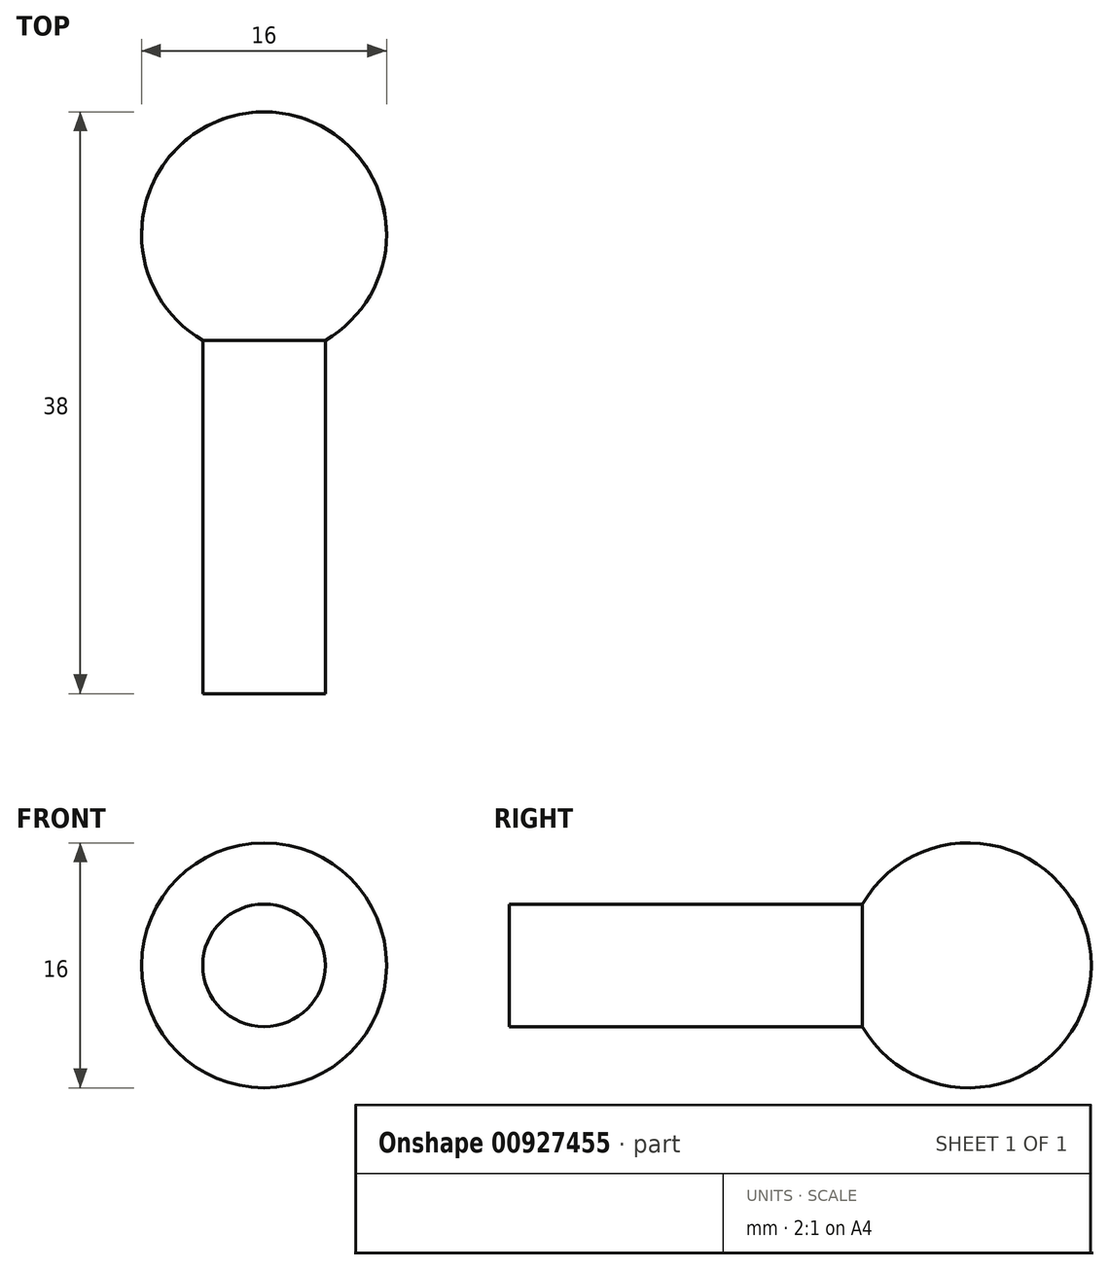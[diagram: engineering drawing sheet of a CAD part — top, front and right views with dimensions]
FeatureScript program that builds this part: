
annotation { "Feature Type Name" : "Feature", "Feature Type Description" : "" }
export const myFeature = defineFeature(function(context is Context, id is Id, definition is map)
    precondition{}
    {
        {
            var Q0;
            Q0=qCreatedBy(makeId("Top.planeOp"),FACE);
            var sketch = newSketch(context, id + "F0", { "sketchPlane" : qUnion([Q0])});
            skArc(sketch, "E0", {"start": v(8, 0) * mm, "mid": v(0, 8) * mm, "end": v(-8, 0) * mm});
            skLineSegment(sketch, "E1", {"start": v(-8, 0) * mm, "end": v(8, 0) * mm});
            skPoint(sketch, "E2.orphan", {"position": v(-57.76, 0) * mm});
            skSolve(sketch);
        }
        {
            var Q0;
            Q0=makeQuery(id+"F0.imprint","IMPRINT",FACE,{"disambiguationData":[TD([[makeQuery(id+"F0.imprint","IMPRINT",EDGE,{"derivedFrom":sQuery(id+"F0.wireOp",EDGE,"E0")}),1.0]])]});
            var Q1;
            Q1=sQuery(id+"F0.wireOp",EDGE,"E1");
            revolve(context, id + "F1", {"surfaceOperationType" : NewSurfaceOperationType.NEW, "entities" : qUnion([Q0]), "axis" : qUnion([Q1]), "revolveType" : RevolveType.FULL});
        }
        {
            var Q0;
            Q0=qCreatedBy(makeId("Top.planeOp"),FACE);
            var sketch = newSketch(context, id + "F2", { "sketchPlane" : qUnion([Q0])});
            skLineSegment(sketch, "E3", {"start": v(0, 0) * mm, "end": v(0, -30) * mm});
            skLineSegment(sketch, "E4", {"start": v(0, -30) * mm, "end": v(4, -30) * mm});
            skLineSegment(sketch, "E5", {"start": v(4, -30) * mm, "end": v(4, 0) * mm});
            skLineSegment(sketch, "E6", {"start": v(4, 0) * mm, "end": v(0, 0) * mm});
            skSolve(sketch);
        }
        {
            var Q0;
            Q0=makeQuery(id+"F2.imprint","IMPRINT",FACE,{"disambiguationData":[TD([[makeQuery(id+"F2.imprint","IMPRINT",EDGE,{"derivedFrom":sQuery(id+"F2.wireOp",EDGE,"E3")}),1.0]])]});
            var Q1;
            Q1=sQuery(id+"F2.wireOp",EDGE,"E3");
            revolve(context, id + "F3", {"operationType" : NewBodyOperationType.ADD, "surfaceOperationType" : NewSurfaceOperationType.NEW, "entities" : qUnion([Q0]), "axis" : qUnion([Q1]), "revolveType" : RevolveType.FULL});
        }
    });
